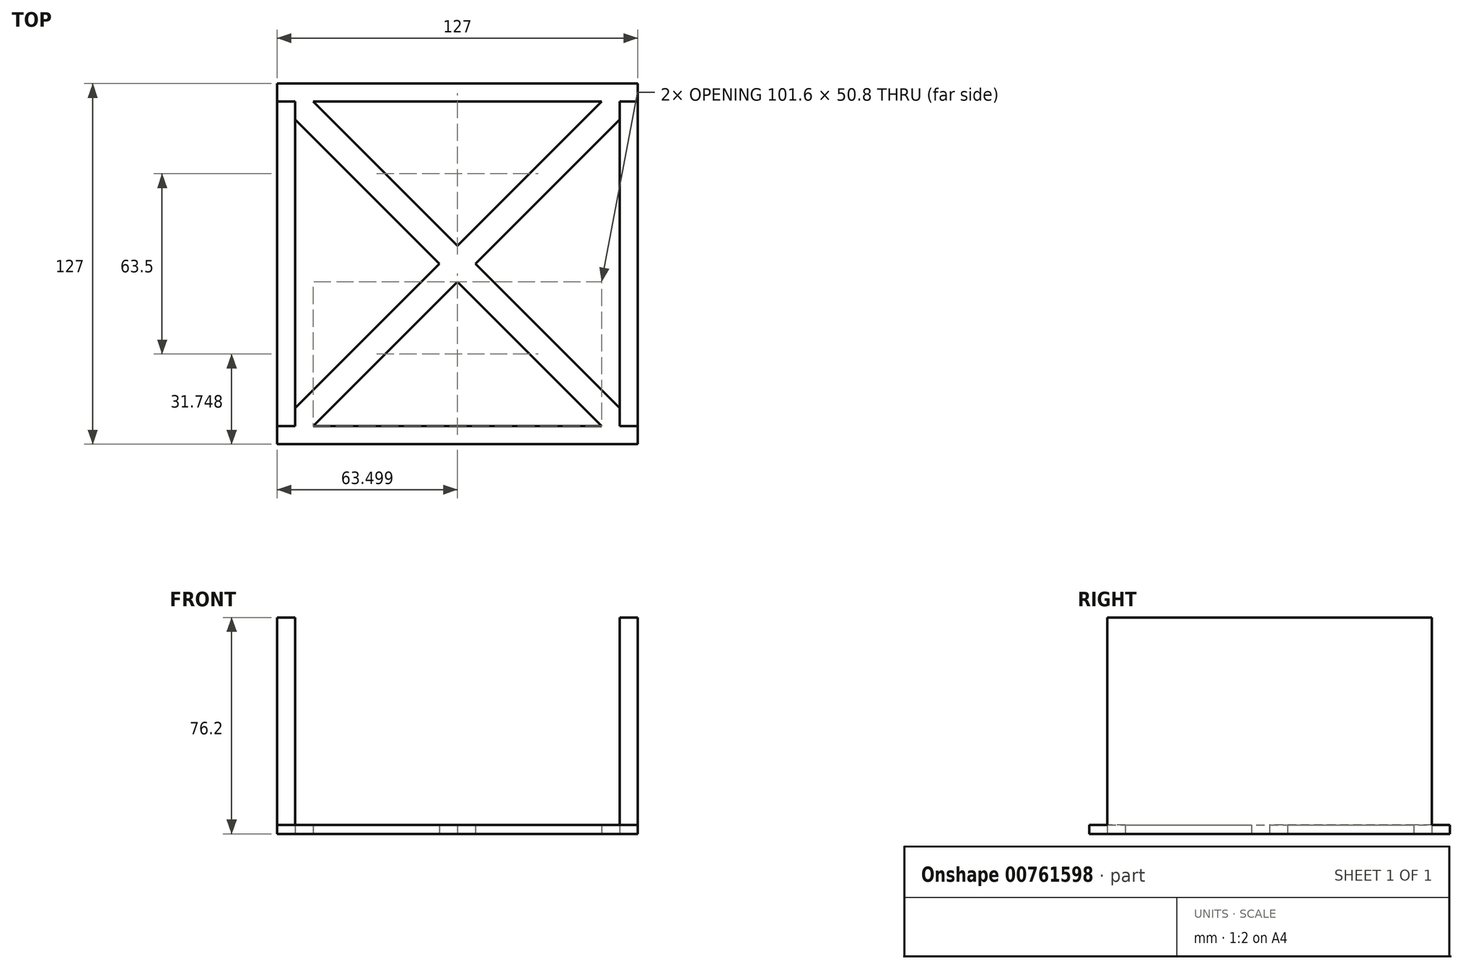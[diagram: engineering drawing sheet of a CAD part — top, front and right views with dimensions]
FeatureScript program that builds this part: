
annotation { "Feature Type Name" : "Feature", "Feature Type Description" : "" }
export const myFeature = defineFeature(function(context is Context, id is Id, definition is map)
    precondition{}
    {
        {
            var Q0;
            Q0=qCreatedBy(makeId("Top.planeOp"),FACE);
            var sketch = newSketch(context, id + "F0", { "sketchPlane" : qUnion([Q0])});
            skLineSegment(sketch, "E0.bottom", {"start": v(-93.65, 35.95) * mm, "end": v(20.65, 35.95) * mm});
            skLineSegment(sketch, "E0.top", {"start": v(-93.65, -78.35) * mm, "end": v(20.65, -78.35) * mm});
            skLineSegment(sketch, "E0.left", {"start": v(-93.65, 35.95) * mm, "end": v(-93.65, -78.35) * mm});
            skLineSegment(sketch, "E0.right", {"start": v(20.65, 35.95) * mm, "end": v(20.65, -78.35) * mm});
            skLineSegment(sketch, "E1.bottom", {"start": v(20.65, 35.95) * mm, "end": v(20.65, 35.95) * mm});
            skLineSegment(sketch, "E1.top", {"start": v(20.65, -78.35) * mm, "end": v(20.65, -78.35) * mm});
            skLineSegment(sketch, "E2.bottom", {"start": v(20.65, 35.95) * mm, "end": v(27, 35.95) * mm});
            skLineSegment(sketch, "E2.top", {"start": v(20.65, -78.35) * mm, "end": v(27, -78.35) * mm});
            skLineSegment(sketch, "E2.right", {"start": v(27, 35.95) * mm, "end": v(27, -78.35) * mm});
            skLineSegment(sketch, "E3.bottom", {"start": v(-93.65, 35.95) * mm, "end": v(-100, 35.95) * mm});
            skLineSegment(sketch, "E3.top", {"start": v(-93.65, -78.35) * mm, "end": v(-100, -78.35) * mm});
            skLineSegment(sketch, "E3.right", {"start": v(-100, 35.95) * mm, "end": v(-100, -78.35) * mm});
            skLineSegment(sketch, "E4.left", {"start": v(-93.65, 35.95) * mm, "end": v(-93.64, 29.6) * mm});
            skLineSegment(sketch, "E5.bottom", {"start": v(-93.65, 35.95) * mm, "end": v(-87.3, 35.95) * mm});
            skLineSegment(sketch, "E5.top", {"start": v(-93.65, 29.6) * mm, "end": v(-87.3, 29.6) * mm});
            skLineSegment(sketch, "E5.left", {"start": v(-93.65, 35.95) * mm, "end": v(-93.65, 29.6) * mm});
            skLineSegment(sketch, "E5.right", {"start": v(-87.3, 35.95) * mm, "end": v(-87.3, 29.6) * mm});
            skLineSegment(sketch, "E6.bottom", {"start": v(20.65, -78.35) * mm, "end": v(14.3, -78.35) * mm});
            skLineSegment(sketch, "E6.top", {"start": v(20.65, -72) * mm, "end": v(14.3, -72) * mm});
            skLineSegment(sketch, "E6.left", {"start": v(20.65, -78.35) * mm, "end": v(20.65, -72) * mm});
            skLineSegment(sketch, "E6.right", {"start": v(14.3, -78.35) * mm, "end": v(14.3, -72) * mm});
            skLineSegment(sketch, "E7", {"start": v(-93.64, 29.6) * mm, "end": v(14.3, -78.35) * mm});
            skLineSegment(sketch, "E8", {"start": v(20.65, -72) * mm, "end": v(-87.3, 35.95) * mm});
            skLineSegment(sketch, "E9.bottom", {"start": v(-93.65, -78.35) * mm, "end": v(4.14, -78.35) * mm});
            skLineSegment(sketch, "E10.bottom", {"start": v(-100, -78.35) * mm, "end": v(27, -78.35) * mm});
            skLineSegment(sketch, "E10.top", {"start": v(-100, -84.7) * mm, "end": v(27, -84.7) * mm});
            skLineSegment(sketch, "E10.left", {"start": v(-100, -78.35) * mm, "end": v(-100, -84.7) * mm});
            skLineSegment(sketch, "E10.right", {"start": v(27, -78.35) * mm, "end": v(27, -84.7) * mm});
            skLineSegment(sketch, "E11.bottom", {"start": v(-100, 35.95) * mm, "end": v(27, 35.95) * mm});
            skLineSegment(sketch, "E11.top", {"start": v(-100, 35.95) * mm, "end": v(27, 35.95) * mm});
            skLineSegment(sketch, "E11.left", {"start": v(-100, 35.95) * mm, "end": v(-100, 35.95) * mm});
            skLineSegment(sketch, "E11.right", {"start": v(27, 35.95) * mm, "end": v(27, 35.95) * mm});
            skLineSegment(sketch, "E12.top", {"start": v(-100, 42.3) * mm, "end": v(27, 42.3) * mm});
            skLineSegment(sketch, "E12.left", {"start": v(-100, 35.95) * mm, "end": v(-100, 42.3) * mm});
            skLineSegment(sketch, "E12.right", {"start": v(27, 35.95) * mm, "end": v(27, 42.3) * mm});
            skLineSegment(sketch, "E13.bottom", {"start": v(-93.65, -78.35) * mm, "end": v(-87.3, -78.35) * mm});
            skLineSegment(sketch, "E13.top", {"start": v(-93.65, -72) * mm, "end": v(-87.3, -72) * mm});
            skLineSegment(sketch, "E13.left", {"start": v(-93.65, -78.35) * mm, "end": v(-93.65, -72) * mm});
            skLineSegment(sketch, "E13.right", {"start": v(-87.3, -78.35) * mm, "end": v(-87.3, -72) * mm});
            skLineSegment(sketch, "E14.bottom", {"start": v(20.65, 35.95) * mm, "end": v(14.3, 35.95) * mm});
            skLineSegment(sketch, "E14.top", {"start": v(20.65, 29.6) * mm, "end": v(14.3, 29.6) * mm});
            skLineSegment(sketch, "E14.left", {"start": v(20.65, 35.95) * mm, "end": v(20.65, 29.6) * mm});
            skLineSegment(sketch, "E14.right", {"start": v(14.3, 35.95) * mm, "end": v(14.3, 29.6) * mm});
            skLineSegment(sketch, "E15", {"start": v(-87.3, -78.35) * mm, "end": v(20.65, 29.6) * mm});
            skLineSegment(sketch, "E16", {"start": v(-93.65, -72) * mm, "end": v(14.3, 35.95) * mm});
            skSolve(sketch);
        }
        {
            var Q0;
            {var subQ4=sQuery(id+"F0.wireOp",EDGE,"E13.top");Q0=makeQuery(id+"F0.imprint","IMPRINT",FACE,{"disambiguationData":[TD([[makeQuery(id+"F0.imprint","IMPRINT",EDGE,{"derivedFrom":subQ4}),-1.0]])]});}
            var Q1;
            {var subQ6=sQuery(id+"F0.wireOp",EDGE,"E13.top");Q1=makeQuery(id+"F0.imprint","IMPRINT",FACE,{"disambiguationData":[TD([[makeQuery(id+"F0.imprint","IMPRINT",EDGE,{"derivedFrom":subQ6}),1.0]])]});}
            var Q2;
            {var subQ5=sQuery(id+"F0.wireOp",EDGE,"E6.top");Q2=makeQuery(id+"F0.imprint","IMPRINT",FACE,{"disambiguationData":[TD([[makeQuery(id+"F0.imprint","IMPRINT",EDGE,{"derivedFrom":subQ5}),-1.0]])]});}
            var Q3;
            {var subQ5=sQuery(id+"F0.wireOp",EDGE,"E5.right");Q3=makeQuery(id+"F0.imprint","IMPRINT",FACE,{"disambiguationData":[TD([[makeQuery(id+"F0.imprint","IMPRINT",EDGE,{"derivedFrom":subQ5}),1.0]])]});}
            var Q4;
            {var subQ1=sQuery(id+"F0.wireOp",EDGE,"E14.top");Q4=makeQuery(id+"F0.imprint","IMPRINT",FACE,{"disambiguationData":[TD([[makeQuery(id+"F0.imprint","IMPRINT",EDGE,{"derivedFrom":subQ1}),1.0]])]});}
            var Q5;
            {var subQ4=sQuery(id+"F0.wireOp",EDGE,"E14.top");Q5=makeQuery(id+"F0.imprint","IMPRINT",FACE,{"disambiguationData":[TD([[makeQuery(id+"F0.imprint","IMPRINT",EDGE,{"derivedFrom":subQ4}),-1.0]])]});}
            var Q6;
            {var subQ0=sQuery(id+"F0.wireOp",EDGE,"E15");var subQ1=sQuery(id+"F0.wireOp",EDGE,"E7");var subQ2=makeQuery(id+"F0.imprint","INTERSECT",VERTEX,{"derivedFrom":[subQ1,subQ0]});Q6=makeQuery(id+"F0.imprint","IMPRINT",FACE,{"disambiguationData":[TD([[makeQuery(id+"F0.imprint","IMPRINT",EDGE,{"disambiguationData":[TD([[subQ2,1.0]])],"derivedFrom":subQ1}),1.0]])]});}
            var Q7;
            {var subQ0=sQuery(id+"F0.wireOp",EDGE,"E5.right");Q7=makeQuery(id+"F0.imprint","IMPRINT",FACE,{"disambiguationData":[TD([[makeQuery(id+"F0.imprint","IMPRINT",EDGE,{"derivedFrom":subQ0}),-1.0]])]});}
            var Q8;
            {var subQ4=sQuery(id+"F0.wireOp",EDGE,"E6.top");Q8=makeQuery(id+"F0.imprint","IMPRINT",FACE,{"disambiguationData":[TD([[makeQuery(id+"F0.imprint","IMPRINT",EDGE,{"derivedFrom":subQ4}),1.0]])]});}
            var Q9;
            {var subQ0=sQuery(id+"F0.wireOp",EDGE,"E2.bottom");Q9=makeQuery(id+"F0.imprint","IMPRINT",FACE,{"disambiguationData":[TD([[makeQuery(id+"F0.imprint","IMPRINT",EDGE,{"derivedFrom":subQ0}),1.0]])]});}
            var Q10;
            {var subQ3=sQuery(id+"F0.wireOp",EDGE,"E2.top");Q10=makeQuery(id+"F0.imprint","IMPRINT",FACE,{"disambiguationData":[TD([[makeQuery(id+"F0.imprint","IMPRINT",EDGE,{"derivedFrom":subQ3}),-1.0]])]});}
            extrude(context, id + "F1", {"entities" : qUnion([Q0, Q1, Q2, Q3, Q4, Q5, Q6, Q7, Q8, Q9, Q10]), "depth" : 3.17 * mm, "offsetDistance" : 25.4 * mm});
        }
        {
            var Q0;
            {var subQ0=sQuery(id+"F0.wireOp",EDGE,"E3.bottom");Q0=makeQuery(id+"F0.imprint","IMPRINT",FACE,{"disambiguationData":[TD([[makeQuery(id+"F0.imprint","IMPRINT",EDGE,{"derivedFrom":subQ0}),1.0]])]});}
            extrude(context, id + "F2", {"entities" : qUnion([Q0]), "depth" : 76.2 * mm, "offsetDistance" : 25.4 * mm});
        }
        {
            var Q0;
            {var subQ0=sQuery(id+"F0.wireOp",EDGE,"E2.bottom");Q0=makeQuery(id+"F0.imprint","IMPRINT",FACE,{"disambiguationData":[TD([[makeQuery(id+"F0.imprint","IMPRINT",EDGE,{"derivedFrom":subQ0}),-1.0]])]});}
            var Q1;
            Q1=sQuery(id+"F0.wireOp",EDGE,"E0.right");
            extrude(context, id + "F3", {"entities" : qUnion([Q0]), "operationType" : NewBodyOperationType.ADD, "surfaceEntities" : qUnion([Q1]), "depth" : 76.2 * mm, "offsetDistance" : 25.4 * mm});
        }
    });
